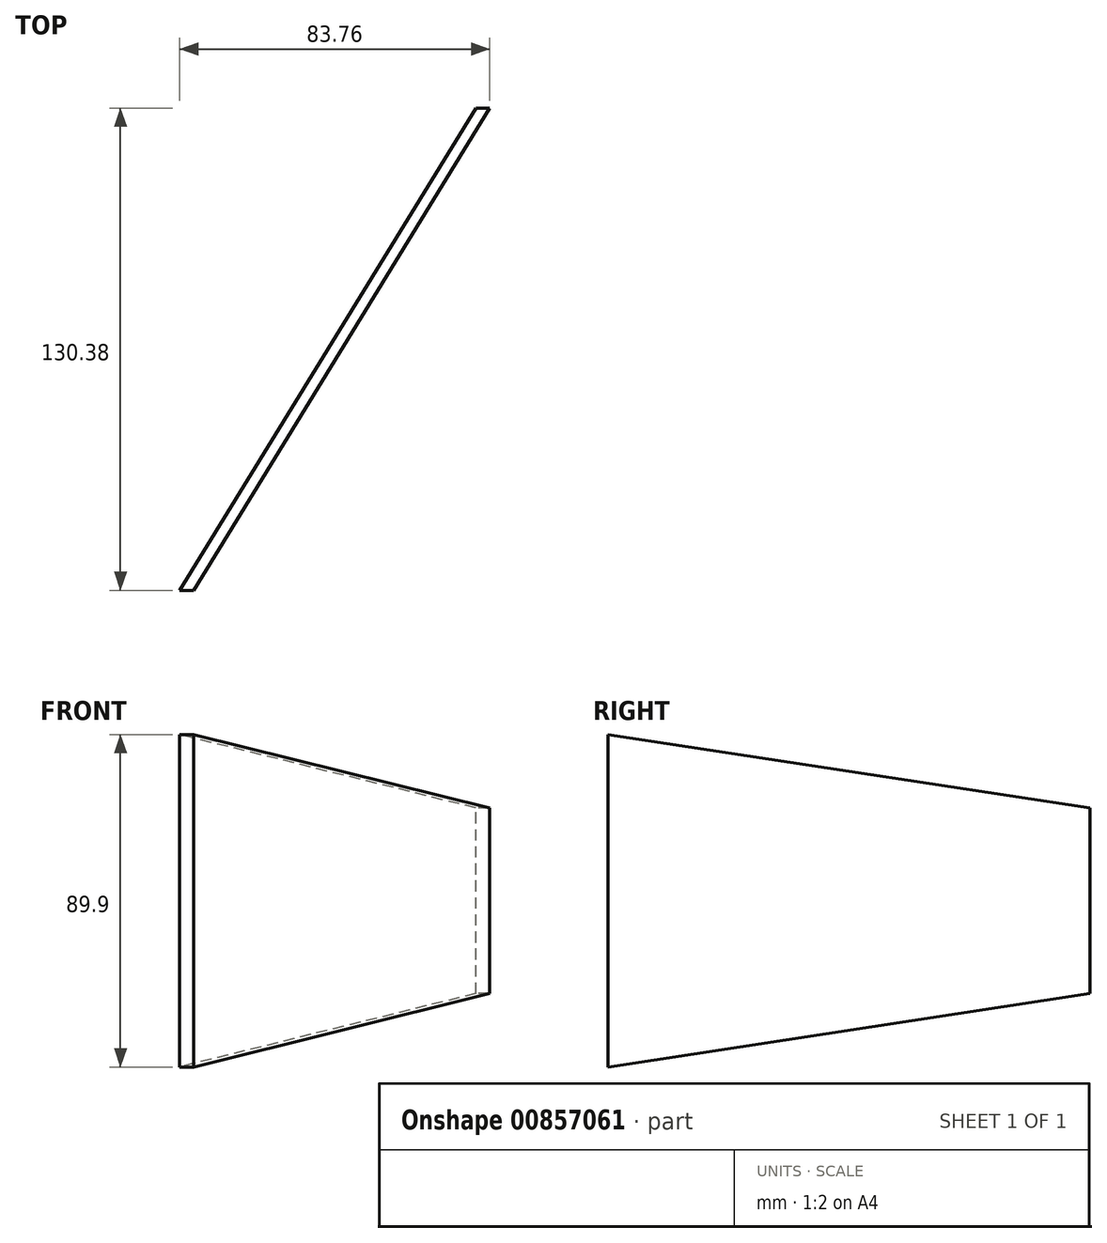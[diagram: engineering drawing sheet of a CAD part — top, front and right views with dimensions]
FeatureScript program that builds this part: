
annotation { "Feature Type Name" : "Feature", "Feature Type Description" : "" }
export const myFeature = defineFeature(function(context is Context, id is Id, definition is map)
    precondition{}
    {
        {
            var Q0;
            Q0=qCreatedBy(makeId("Right.planeOp"),FACE);
            var sketch = newSketch(context, id + "F0", { "sketchPlane" : qUnion([Q0])});
            skLineSegment(sketch, "E0", {"start": v(0, 48.82) * mm, "end": v(0, -48.82) * mm});
            skLineSegment(sketch, "E1", {"start": v(25.4, 44.95) * mm, "end": v(25.4, -44.95) * mm});
            skLineSegment(sketch, "E2", {"start": v(155.78, 25.1) * mm, "end": v(155.78, -25.1) * mm});
            skCircle(sketch, "E3", {"center": v(311.35, 0) * mm, "radius": 1.39 * mm});
            skLineSegment(sketch, "E4", {"start": v(0, 48.82) * mm, "end": v(311.56, 1.37) * mm});
            skLineSegment(sketch, "E5", {"start": v(0, -48.82) * mm, "end": v(311.56, -1.37) * mm});
            skSolve(sketch);
        }
        {
            var Q0;
            {var subQ5=sQuery(id+"F0.wireOp",EDGE,"E2");Q0=makeQuery(id+"F0.imprint","IMPRINT",FACE,{"disambiguationData":[TD([[makeQuery(id+"F0.imprint","IMPRINT",EDGE,{"derivedFrom":subQ5}),-1.0]])]});}
            extrude(context, id + "F1", {"entities" : qUnion([Q0]), "depth" : 254 * mm, "offsetDistance" : 25.4 * mm, "symmetric" : true});
        }
        {
            var Q0;
            Q0=qCreatedBy(makeId("Top.planeOp"),FACE);
            var sketch = newSketch(context, id + "F2", { "sketchPlane" : qUnion([Q0])});
            skLineSegment(sketch, "E6", {"start": v(-182.56, 291.34) * mm, "end": v(182.56, 291.34) * mm});
            skLineSegment(sketch, "E7", {"start": v(0, 0) * mm, "end": v(0, 291.34) * mm});
            skLineSegment(sketch, "E8", {"start": v(-182.56, 291.34) * mm, "end": v(-3.73, 0) * mm});
            skLineSegment(sketch, "E9", {"start": v(0, 0) * mm, "end": v(-178.84, 291.34) * mm});
            skLineSegment(sketch, "E10", {"start": v(-3.73, 0) * mm, "end": v(0, 0) * mm});
            skLineSegment(sketch, "E11", {"start": v(0, 0) * mm, "end": v(178.84, 291.34) * mm});
            skLineSegment(sketch, "E12", {"start": v(182.56, 291.34) * mm, "end": v(3.73, 0) * mm});
            skLineSegment(sketch, "E13", {"start": v(3.73, 0) * mm, "end": v(0, 0) * mm});
            skSolve(sketch);
        }
        {
            var Q0;
            {var subQ2=sQuery(id+"F2.wireOp",EDGE,"E11");Q0=makeQuery(id+"F2.imprint","IMPRINT",FACE,{"disambiguationData":[TD([[makeQuery(id+"F2.imprint","IMPRINT",EDGE,{"derivedFrom":subQ2}),-1.0]])]});}
            extrude(context, id + "F3", {"entities" : qUnion([Q0]), "operationType" : NewBodyOperationType.INTERSECT, "depth" : 101.6 * mm, "offsetDistance" : 25.4 * mm, "symmetric" : true});
        }
    });
